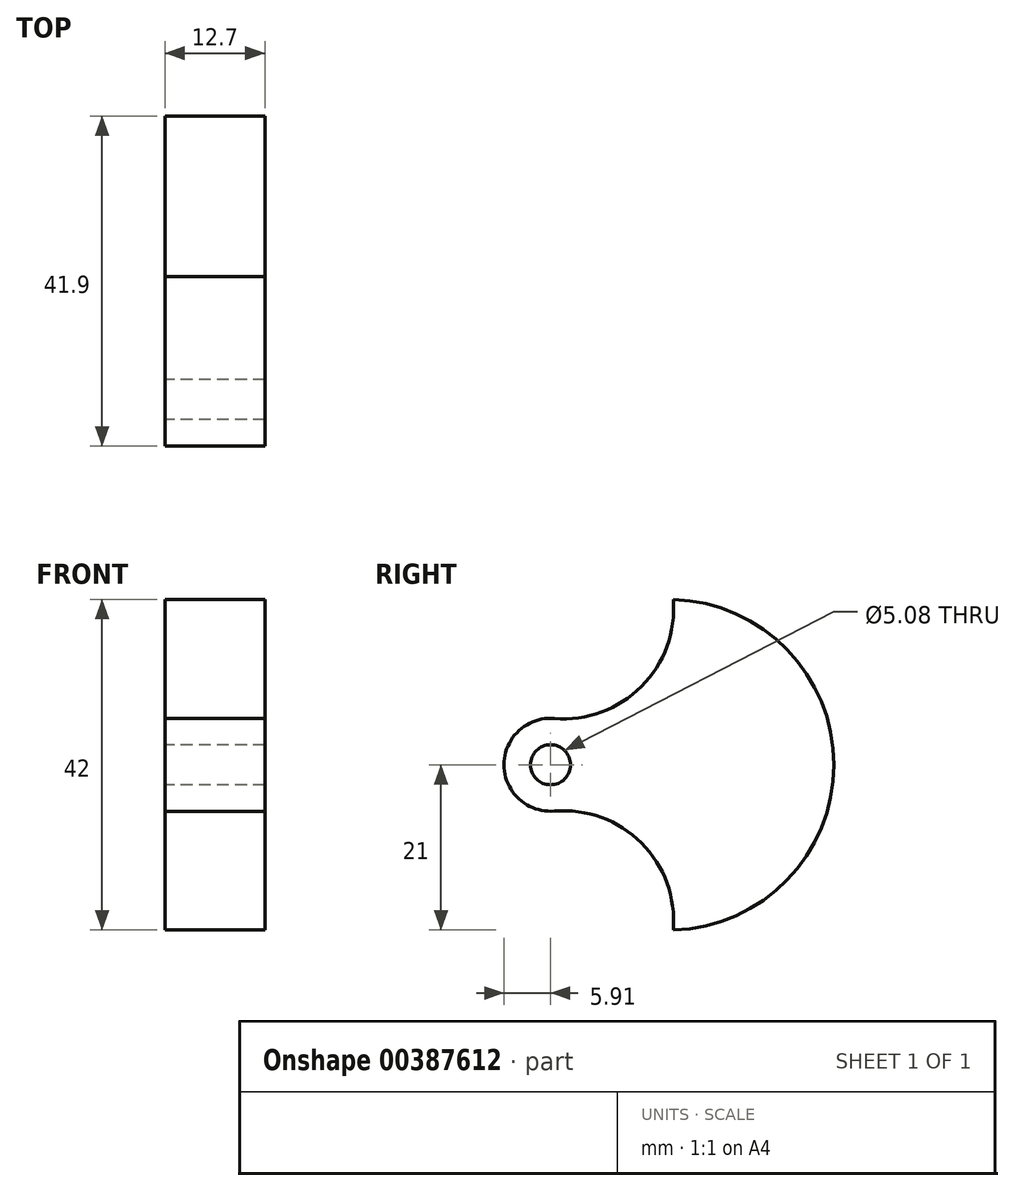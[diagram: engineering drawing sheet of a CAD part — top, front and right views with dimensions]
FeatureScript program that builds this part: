
annotation { "Feature Type Name" : "Feature", "Feature Type Description" : "" }
export const myFeature = defineFeature(function(context is Context, id is Id, definition is map)
    precondition{}
    {
        {
            var Q0;
            Q0=qCreatedBy(makeId("Right.planeOp"),FACE);
            var sketch = newSketch(context, id + "F0", { "sketchPlane" : qUnion([Q0])});
            skLineSegment(sketch, "E0", {"start": v(0, 0) * mm, "end": v(36, 0) * mm});
            skCircle(sketch, "E1", {"center": v(14.99, 0) * mm, "radius": 21 * mm});
            skCircle(sketch, "E2", {"center": v(0, 0) * mm, "radius": 2.54 * mm});
            skLineSegment(sketch, "E3", {"start": v(0, 0) * mm, "end": v(-5.9, 0) * mm});
            skCircle(sketch, "E4", {"center": v(0, 0) * mm, "radius": 5.9 * mm});
            skCircle(sketch, "E5", {"center": v(1.65, 19.83) * mm, "radius": 14 * mm});
            skCircle(sketch, "E6.MirrorC", {"center": v(1.65, -19.83) * mm, "radius": 14 * mm});
            skSolve(sketch);
        }
        {
            var Q0;
            {var subQ0=sQuery(id+"F0.wireOp",EDGE,"E1");var subQ1=sQuery(id+"F0.wireOp",EDGE,"E0");var subQ2=makeQuery(id+"F0.imprint","INTERSECT",VERTEX,{"derivedFrom":[subQ1,subQ0]});Q0=makeQuery(id+"F0.imprint","IMPRINT",FACE,{"disambiguationData":[TD([[makeQuery(id+"F0.imprint","IMPRINT",EDGE,{"disambiguationData":[TD([[subQ2,1.0]])],"derivedFrom":subQ1}),1.0]])]});}
            var Q1;
            {var subQ0=sQuery(id+"F0.wireOp",EDGE,"E1");var subQ1=sQuery(id+"F0.wireOp",EDGE,"E0");var subQ2=makeQuery(id+"F0.imprint","INTERSECT",VERTEX,{"derivedFrom":[subQ1,subQ0]});Q1=makeQuery(id+"F0.imprint","IMPRINT",FACE,{"disambiguationData":[TD([[makeQuery(id+"F0.imprint","IMPRINT",EDGE,{"disambiguationData":[TD([[subQ2,1.0]])],"derivedFrom":subQ1}),-1.0]])]});}
            var Q2;
            {var subQ4=sQuery(id+"F0.wireOp",EDGE,"E2");var subQ5=sQuery(id+"F0.wireOp",EDGE,"E0");var subQ6=makeQuery(id+"F0.imprint","INTERSECT",VERTEX,{"derivedFrom":[subQ5,subQ4]});Q2=makeQuery(id+"F0.imprint","IMPRINT",FACE,{"disambiguationData":[TD([[makeQuery(id+"F0.imprint","IMPRINT",EDGE,{"disambiguationData":[TD([[subQ6,-1.0]])],"derivedFrom":subQ5}),-1.0]])]});}
            var Q3;
            {var subQ1=sQuery(id+"F0.wireOp",EDGE,"E0");var subQ4=sQuery(id+"F0.wireOp",EDGE,"E2");var subQ5=makeQuery(id+"F0.imprint","INTERSECT",VERTEX,{"derivedFrom":[subQ1,subQ4]});Q3=makeQuery(id+"F0.imprint","IMPRINT",FACE,{"disambiguationData":[TD([[makeQuery(id+"F0.imprint","IMPRINT",EDGE,{"disambiguationData":[TD([[subQ5,-1.0]])],"derivedFrom":subQ1}),1.0]])]});}
            extrude(context, id + "F1", {"entities" : qUnion([Q0, Q1, Q2, Q3]), "depth" : 12.7 * mm});
        }
    });
